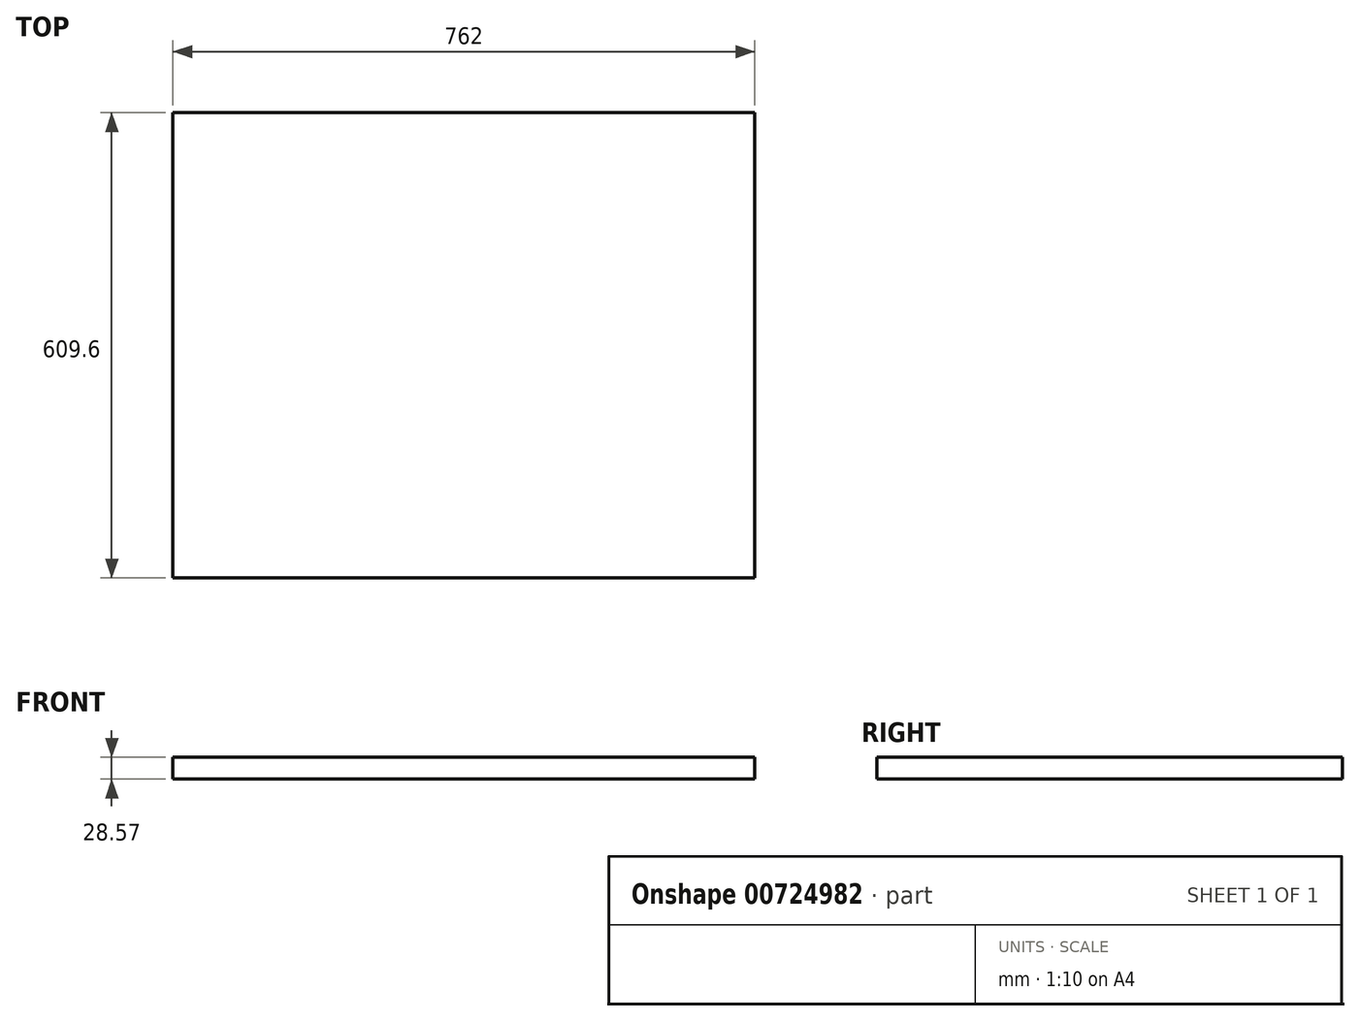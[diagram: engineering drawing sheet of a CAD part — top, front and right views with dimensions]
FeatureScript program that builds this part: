
annotation { "Feature Type Name" : "Feature", "Feature Type Description" : "" }
export const myFeature = defineFeature(function(context is Context, id is Id, definition is map)
    precondition{}
    {
        {
            var Q0;
            Q0=qCreatedBy(makeId("Top.planeOp"),FACE);
            var sketch = newSketch(context, id + "F0", { "sketchPlane" : qUnion([Q0])});
            skLineSegment(sketch, "E0.bottom", {"start": v(381, 304.8) * mm, "end": v(-381, 304.8) * mm});
            skLineSegment(sketch, "E0.top", {"start": v(381, -304.8) * mm, "end": v(-381, -304.8) * mm});
            skLineSegment(sketch, "E0.left", {"start": v(381, 304.8) * mm, "end": v(381, -304.8) * mm});
            skLineSegment(sketch, "E0.right", {"start": v(-381, 304.8) * mm, "end": v(-381, -304.8) * mm});
            skPoint(sketch, "E0.middle", {"position": v(0, 0) * mm});
            skSolve(sketch);
        }
        {
            var Q0;
            Q0=makeQuery(id+"F0.imprint","IMPRINT",FACE,{"disambiguationData":[TD([[makeQuery(id+"F0.imprint","IMPRINT",EDGE,{"derivedFrom":sQuery(id+"F0.wireOp",EDGE,"E0.bottom")}),1.0]])]});
            extrude(context, id + "F1", {"entities" : qUnion([Q0]), "depth" : 28.57 * mm, "offsetDistance" : 25.4 * mm});
        }
    });
